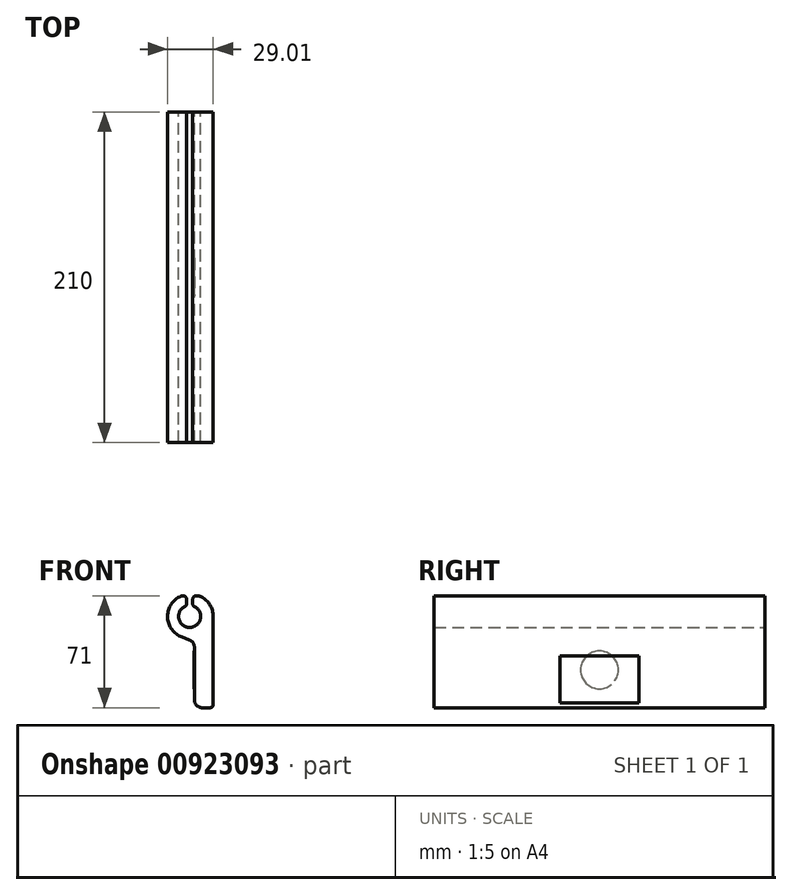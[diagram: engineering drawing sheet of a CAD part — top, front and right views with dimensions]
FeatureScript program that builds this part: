
annotation { "Feature Type Name" : "Feature", "Feature Type Description" : "" }
export const myFeature = defineFeature(function(context is Context, id is Id, definition is map)
    precondition{}
    {
        {
            var Q0;
            Q0=qCreatedBy(makeId("Front.planeOp"),FACE);
            var sketch = newSketch(context, id + "F0", { "sketchPlane" : qUnion([Q0])});
            skArc(sketch, "E0", {"start": v(2.5, -30.5) * mm, "mid": v(3.96, -34.04) * mm, "end": v(7.5, -35.5) * mm});
            skLineSegment(sketch, "E1", {"start": v(7.5, -35.5) * mm, "end": v(12.5, -35.5) * mm});
            skArc(sketch, "E2", {"start": v(12.5, -35.5) * mm, "mid": v(13.91, -34.91) * mm, "end": v(14.5, -33.5) * mm});
            skLineSegment(sketch, "E3", {"start": v(14.5, -33.5) * mm, "end": v(14.5, 22.5) * mm});
            skArc(sketch, "E4", {"start": v(14.5, 22.5) * mm, "mid": v(12.45, 29.79) * mm, "end": v(6.91, 34.94) * mm});
            skArc(sketch, "E5", {"start": v(6.91, 34.94) * mm, "mid": v(5.8, 35.36) * mm, "end": v(4.62, 35.5) * mm});
            skLineSegment(sketch, "E6", {"start": v(4.62, 35.5) * mm, "end": v(3.5, 35.5) * mm});
            skArc(sketch, "E7", {"start": v(3.5, 35.5) * mm, "mid": v(2.09, 34.91) * mm, "end": v(1.5, 33.5) * mm});
            skLineSegment(sketch, "E8", {"start": v(1.5, 33.5) * mm, "end": v(1.5, 30.25) * mm});
            skArc(sketch, "E9", {"start": v(1.5, 30.25) * mm, "mid": v(1.74, 29.43) * mm, "end": v(2.38, 28.88) * mm});
            skArc(sketch, "E10", {"start": v(-3.38, 28.88) * mm, "mid": v(-0.5, 15.5) * mm, "end": v(2.38, 28.88) * mm});
            skArc(sketch, "E11", {"start": v(-3.38, 28.88) * mm, "mid": v(-2.74, 29.43) * mm, "end": v(-2.5, 30.25) * mm});
            skLineSegment(sketch, "E12", {"start": v(-2.5, 30.25) * mm, "end": v(-2.5, 33.5) * mm});
            skArc(sketch, "E13", {"start": v(-2.5, 33.5) * mm, "mid": v(-3.09, 34.91) * mm, "end": v(-4.5, 35.5) * mm});
            skLineSegment(sketch, "E14", {"start": v(-4.5, 35.5) * mm, "end": v(-4.62, 35.5) * mm});
            skArc(sketch, "E15", {"start": v(-4.62, 35.5) * mm, "mid": v(-5.8, 35.36) * mm, "end": v(-6.91, 34.94) * mm});
            skArc(sketch, "E16", {"start": v(-6.91, 34.94) * mm, "mid": v(-14.47, 21.61) * mm, "end": v(-5.29, 9.34) * mm});
            skLineSegment(sketch, "E17", {"start": v(-5.29, 9.34) * mm, "end": v(-0.79, 7.7) * mm});
            skArc(sketch, "E18", {"start": v(2.5, 3) * mm, "mid": v(1.6, 5.88) * mm, "end": v(-0.79, 7.7) * mm});
            skLineSegment(sketch, "E19", {"start": v(2.5, 3) * mm, "end": v(2.5, -30.5) * mm});
            skLineSegment(sketch, "E20", {"start": v(4.5, -23.5) * mm, "end": v(4.4, -23.5) * mm});
            skSolve(sketch);
        }
        {
            var Q0;
            {var subQ0=sQuery(id+"F0.wireOp",EDGE,"E0");Q0=makeQuery(id+"F0.imprint","IMPRINT",FACE,{"disambiguationData":[TD([[makeQuery(id+"F0.imprint","IMPRINT",EDGE,{"derivedFrom":subQ0}),1.0]])]});}
            extrude(context, id + "F1", {"entities" : qUnion([Q0]), "endBound" : BoundingType.SYMMETRIC, "depth" : 210 * mm, "offsetDistance" : 25 * mm});
        }
        {
            var Q0;
            Q0=makeQuery(id+"F1.opExtrude","SWEPT_FACE",FACE,{"disambiguationData":[OSD([sQuery(id+"F0.wireOp",EDGE,"E19")])]});
            var sketch = newSketch(context, id + "F2", { "sketchPlane" : qUnion([Q0])});
            skCircle(sketch, "E21", {"center": v(0, -11.5) * mm, "radius": 12 * mm});
            skSolve(sketch);
        }
        {
            var Q0;
            Q0=makeQuery(id+"F2.imprint","IMPRINT",FACE,{"disambiguationData":[TD([[makeQuery(id+"F2.imprint","IMPRINT",EDGE,{"derivedFrom":sQuery(id+"F2.wireOp",EDGE,"E21")}),1.0]])]});
            extrude(context, id + "F3", {"entities" : qUnion([Q0]), "operationType" : NewBodyOperationType.ADD, "depth" : 0.05 * mm, "offsetDistance" : 25 * mm});
        }
        {
            var Q0;
            Q0=makeQuery(id+"F1.opExtrude","SWEPT_FACE",FACE,{"disambiguationData":[OSD([sQuery(id+"F0.wireOp",EDGE,"E3")])]});
            var sketch = newSketch(context, id + "F4", { "sketchPlane" : qUnion([Q0])});
            skLineSegment(sketch, "E22.bottom", {"start": v(25, -2.5) * mm, "end": v(-25, -2.5) * mm});
            skLineSegment(sketch, "E22.top", {"start": v(25, -32.5) * mm, "end": v(-25, -32.5) * mm});
            skLineSegment(sketch, "E22.left", {"start": v(25, -2.5) * mm, "end": v(25, -32.5) * mm});
            skLineSegment(sketch, "E22.right", {"start": v(-25, -2.5) * mm, "end": v(-25, -32.5) * mm});
            skPoint(sketch, "E22.middle", {"position": v(0, -17.5) * mm});
            skPoint(sketch, "E22.middle.positionSnap0", {"position": v(0, -33.5) * mm});
            skPoint(sketch, "E22.centerSnap0", {"position": v(0, -33.5) * mm});
            skSolve(sketch);
        }
        {
            var Q0;
            Q0=makeQuery(id+"F4.imprint","IMPRINT",FACE,{"disambiguationData":[TD([[makeQuery(id+"F4.imprint","IMPRINT",EDGE,{"derivedFrom":sQuery(id+"F4.wireOp",EDGE,"E22.bottom")}),1.0]])]});
            extrude(context, id + "F5", {"entities" : qUnion([Q0]), "operationType" : NewBodyOperationType.ADD, "depth" : 0.01 * mm, "offsetDistance" : 25 * mm});
        }
    });
